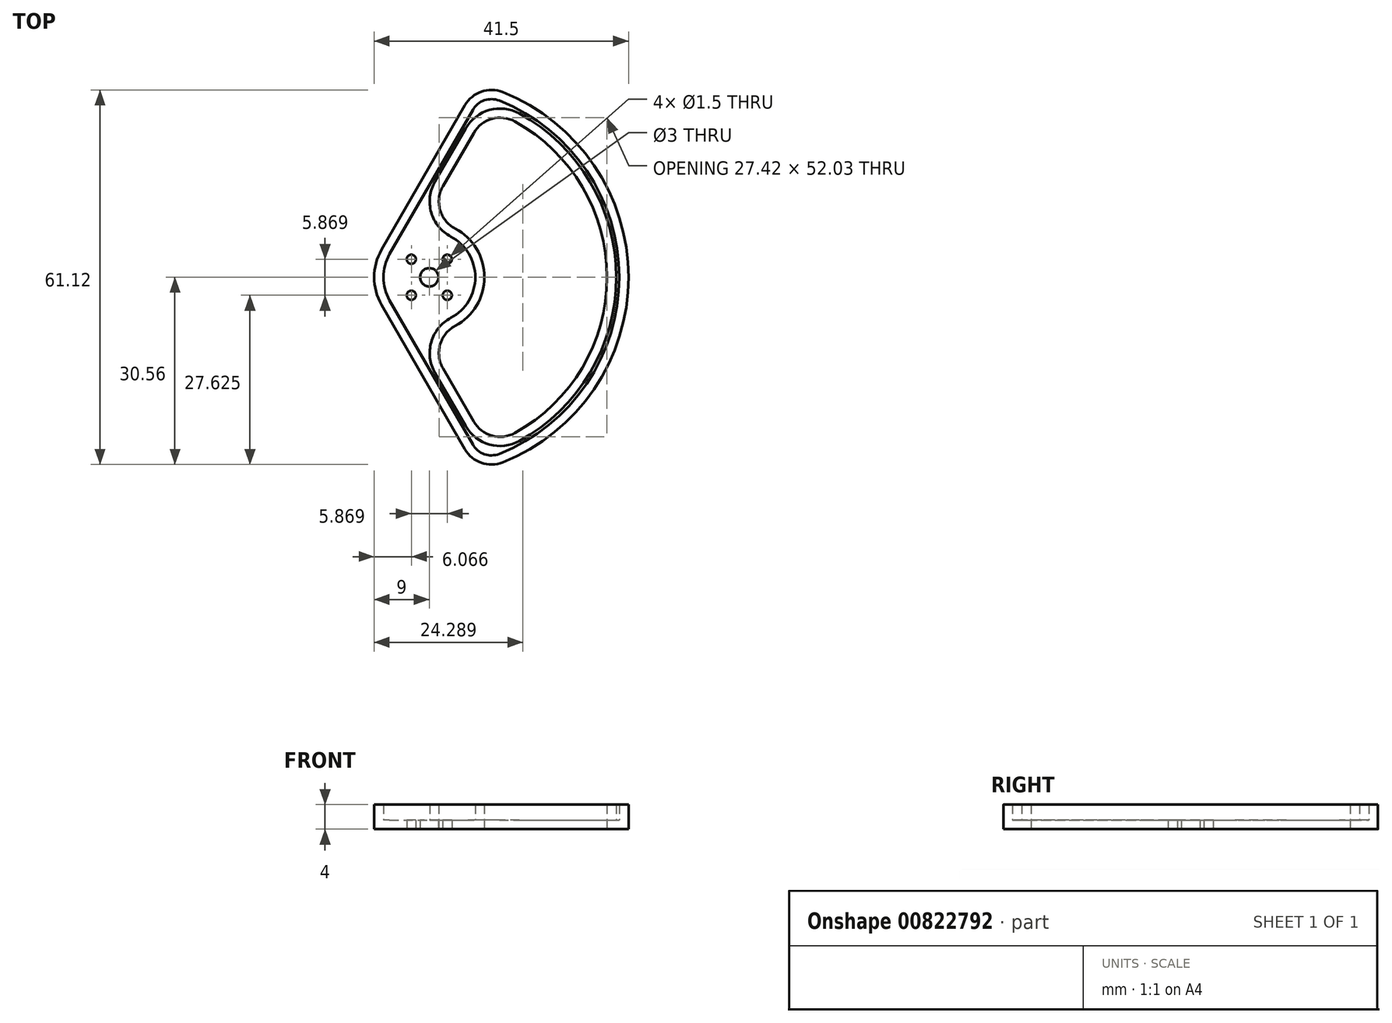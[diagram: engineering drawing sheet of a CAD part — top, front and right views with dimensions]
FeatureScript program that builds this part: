
annotation { "Feature Type Name" : "Feature", "Feature Type Description" : "" }
export const myFeature = defineFeature(function(context is Context, id is Id, definition is map)
    precondition{}
    {
        {
            var Q0;
            Q0=qCreatedBy(makeId("Top.planeOp"),FACE);
            var sketch = newSketch(context, id + "F0", { "sketchPlane" : qUnion([Q0])});
            skCircle(sketch, "E0", {"center": v(0, 0) * mm, "radius": 9 * mm});
            skArc(sketch, "E1", {"start": v(7.82, -31.55) * mm, "mid": v(32.5, 0) * mm, "end": v(7.82, 31.55) * mm});
            skLineSegment(sketch, "E2", {"start": v(-7.8, 4.5) * mm, "end": v(7.82, 31.55) * mm});
            skLineSegment(sketch, "E3.MirrorCS", {"start": v(-7.8, -4.5) * mm, "end": v(7.82, -31.55) * mm});
            skLineSegment(sketch, "E4.0", {"start": v(-1.2, -8.92) * mm, "end": v(9.47, -27.4) * mm});
            skArc(sketch, "E4.1", {"start": v(9.47, -27.4) * mm, "mid": v(29, 0) * mm, "end": v(9.47, 27.4) * mm});
            skLineSegment(sketch, "E4.2", {"start": v(-1.2, 8.92) * mm, "end": v(9.47, 27.4) * mm});
            skSolve(sketch);
        }
        {
            var Q0;
            Q0=makeQuery(id+"F0.imprint","IMPRINT",FACE,{"disambiguationData":[TD([[makeQuery(id+"F0.imprint","IMPRINT",EDGE,{"derivedFrom":sQuery(id+"F0.wireOp",EDGE,"E1")}),1.0]])]});
            var Q1;
            {var subQ0=sQuery(id+"F0.wireOp",EDGE,"E0");var subQ1=makeQuery(id+"F0.imprint","INTERSECT",VERTEX,{"derivedFrom":[subQ0,sQuery(id+"F0.wireOp",EDGE,"E2")]});Q1=makeQuery(id+"F0.imprint","IMPRINT",FACE,{"disambiguationData":[TD([[makeQuery(id+"F0.imprint","IMPRINT",EDGE,{"disambiguationData":[TD([[subQ1,1.0]])],"derivedFrom":subQ0}),1.0]])]});}
            extrude(context, id + "F1", {"entities" : qUnion([Q0, Q1]), "depth" : 4 * mm, "offsetDistance" : 25 * mm});
        }
        {
            var Q0;
            Q0=makeQuery(id+"F1.opExtrude","SWEPT_EDGE",EDGE,{"disambiguationData":[OSD([sQuery(id+"F0.wireOp",EDGE,"E4.1"),sQuery(id+"F0.wireOp",EDGE,"E4.2")])]});
            var Q1;
            Q1=makeQuery(id+"F1.opExtrude","SWEPT_EDGE",EDGE,{"disambiguationData":[OSD([sQuery(id+"F0.wireOp",EDGE,"E4.0"),sQuery(id+"F0.wireOp",EDGE,"E4.1")])]});
            var Q2;
            Q2=makeQuery(id+"F1.opExtrude","SWEPT_EDGE",EDGE,{"disambiguationData":[OSD([sQuery(id+"F0.wireOp",EDGE,"E1"),sQuery(id+"F0.wireOp",EDGE,"E2")])]});
            var Q3;
            Q3=makeQuery(id+"F1.opExtrude","SWEPT_EDGE",EDGE,{"disambiguationData":[OSD([sQuery(id+"F0.wireOp",EDGE,"E0"),sQuery(id+"F0.wireOp",EDGE,"E4.0")])]});
            var Q4;
            Q4=makeQuery(id+"F1.opExtrude","SWEPT_EDGE",EDGE,{"disambiguationData":[OSD([sQuery(id+"F0.wireOp",EDGE,"E0"),sQuery(id+"F0.wireOp",EDGE,"E4.2")])]});
            var Q5;
            Q5=makeQuery(id+"F1.opExtrude","SWEPT_EDGE",EDGE,{"disambiguationData":[OSD([sQuery(id+"F0.wireOp",EDGE,"E1"),sQuery(id+"F0.wireOp",EDGE,"E3.MirrorCS")])]});
            fillet(context, id + "F2", {"entities" : qUnion([Q0, Q1, Q2, Q3, Q4, Q5]), "radius" : 5 * mm, "tangentPropagation" : true, "allowEdgeOverflow" : false});
        }
        {
            var Q0;
            Q0=makeQuery(id+"F1.opExtrude","CAP_FACE",FACE,{"disambiguationData":[OSD([sQuery(id+"F0.wireOp",EDGE,"E0"),sQuery(id+"F0.wireOp",EDGE,"E1"),sQuery(id+"F0.wireOp",EDGE,"E2"),sQuery(id+"F0.wireOp",EDGE,"E3.MirrorCS"),sQuery(id+"F0.wireOp",EDGE,"E4.0"),sQuery(id+"F0.wireOp",EDGE,"E4.1"),sQuery(id+"F0.wireOp",EDGE,"E4.2")])],"isStart":false});
            shell(context, id + "F3", {"entities" : qUnion([Q0]), "thickness" : 1.5 * mm});
        }
        {
            var Q0;
            Q0=qCreatedBy(makeId("Top.planeOp"),FACE);
            var sketch = newSketch(context, id + "F4", { "sketchPlane" : qUnion([Q0])});
            skCircle(sketch, "E5", {"center": v(0, 0) * mm, "radius": 1.5 * mm});
            skSolve(sketch);
        }
        {
            var Q0;
            Q0 = qSketchRegion(id + "F4", true);
            extrude(context, id + "F5", {"entities" : qUnion([Q0]), "operationType" : NewBodyOperationType.REMOVE, "depth" : 3 * mm, "offsetDistance" : 25 * mm});
        }
        {
            var Q0;
            Q0=qCreatedBy(makeId("Top.planeOp"),FACE);
            var sketch = newSketch(context, id + "F6", { "sketchPlane" : qUnion([Q0])});
            skCircle(sketch, "E6", {"center": v(2.93, 2.93) * mm, "radius": 0.75 * mm});
            skCircle(sketch, "E7.MirrorC", {"center": v(-2.93, 2.93) * mm, "radius": 0.75 * mm});
            skCircle(sketch, "E8.MirrorC", {"center": v(-2.93, -2.93) * mm, "radius": 0.75 * mm});
            skCircle(sketch, "E9.MirrorC", {"center": v(2.93, -2.93) * mm, "radius": 0.75 * mm});
            skSolve(sketch);
        }
        {
            var Q0;
            Q0 = qSketchRegion(id + "F6", true);
            extrude(context, id + "F7", {"entities" : qUnion([Q0]), "operationType" : NewBodyOperationType.REMOVE, "endBound" : BoundingType.UP_TO_NEXT, "depth" : 25 * mm, "offsetDistance" : 25 * mm});
        }
    });
